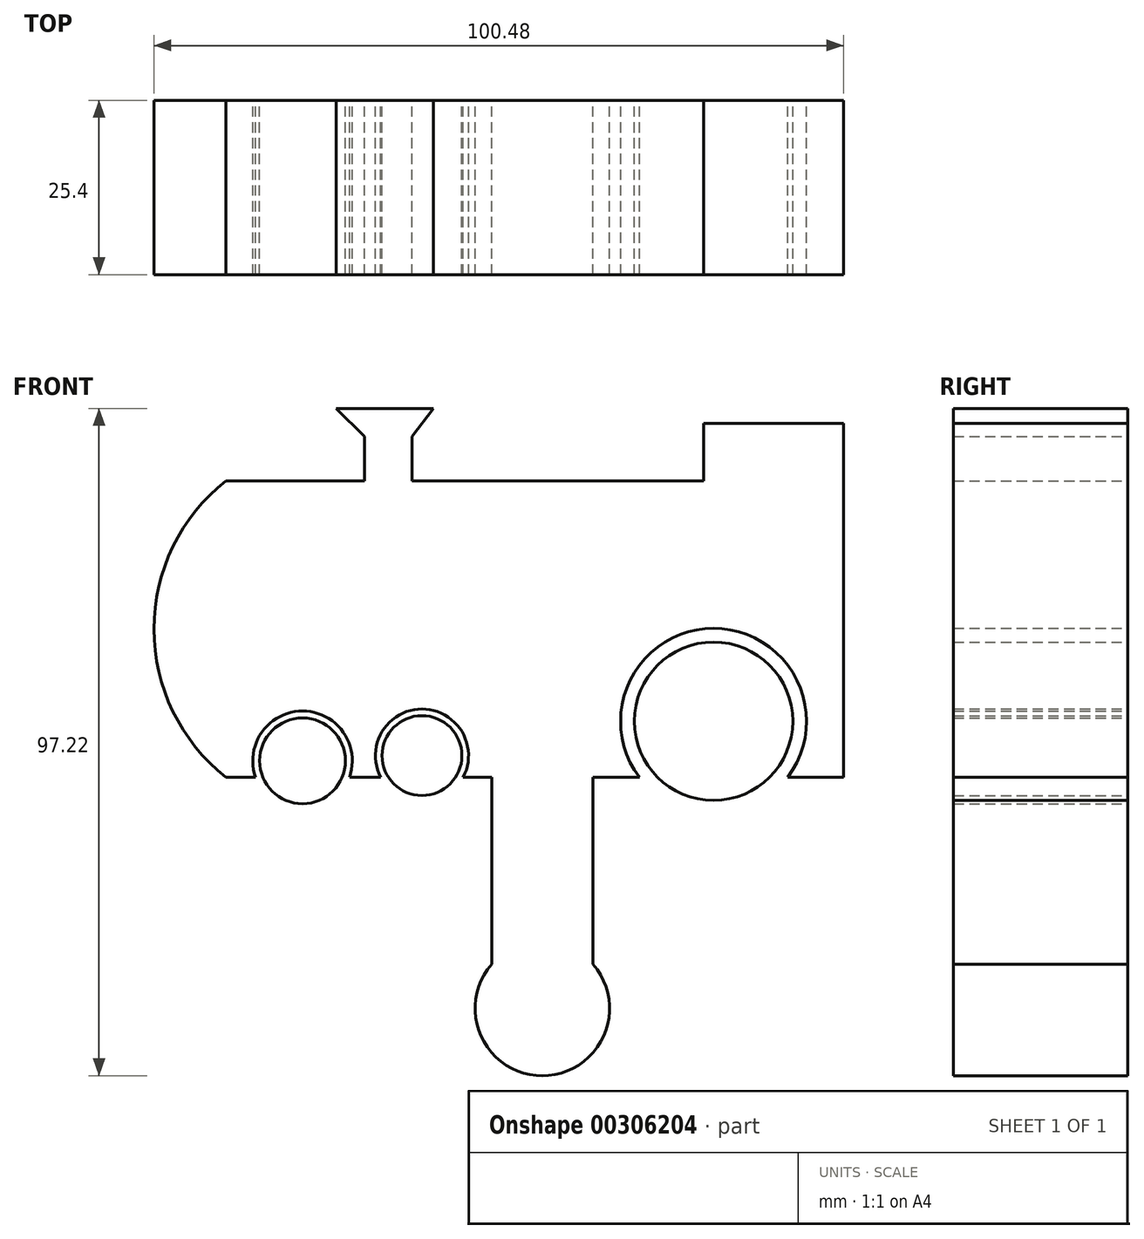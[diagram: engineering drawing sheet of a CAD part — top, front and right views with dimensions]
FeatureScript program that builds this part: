
annotation { "Feature Type Name" : "Feature", "Feature Type Description" : "" }
export const myFeature = defineFeature(function(context is Context, id is Id, definition is map)
    precondition{}
    {
        {
            var Q0;
            Q0=qCreatedBy(makeId("Front.planeOp"),FACE);
            var sketch = newSketch(context, id + "F0", { "sketchPlane" : qUnion([Q0])});
            skLineSegment(sketch, "E0", {"start": v(-7.42, 0) * mm, "end": v(-7.42, -27.23) * mm});
            skLineSegment(sketch, "E1", {"start": v(7.35, 0) * mm, "end": v(7.35, -27.23) * mm});
            skArc(sketch, "E2", {"start": v(-7.42, -27.23) * mm, "mid": v(-0.03, -43.47) * mm, "end": v(7.35, -27.23) * mm});
            skLineSegment(sketch, "E3", {"start": v(-7.42, 0) * mm, "end": v(-11.56, 0) * mm});
            skLineSegment(sketch, "E4", {"start": v(-23.56, 0) * mm, "end": v(-28.12, 0) * mm});
            skLineSegment(sketch, "E5", {"start": v(-41.8, 0) * mm, "end": v(-46.12, 0) * mm});
            skArc(sketch, "E6", {"start": v(-28.12, 0) * mm, "mid": v(-34.96, 9.65) * mm, "end": v(-41.8, 0) * mm});
            skArc(sketch, "E7", {"start": v(-11.56, 0) * mm, "mid": v(-17.56, 9.95) * mm, "end": v(-23.56, 0) * mm});
            skLineSegment(sketch, "E8", {"start": v(7.35, 0) * mm, "end": v(14.12, 0) * mm});
            skLineSegment(sketch, "E9", {"start": v(35.72, 0) * mm, "end": v(43.88, 0) * mm});
            skArc(sketch, "E10", {"start": v(35.72, 0) * mm, "mid": v(24.92, 21.7) * mm, "end": v(14.12, 0) * mm});
            skCircle(sketch, "E11", {"center": v(-34.96, 2.4) * mm, "radius": 6.25 * mm});
            skCircle(sketch, "E12", {"center": v(-17.56, 3.16) * mm, "radius": 5.82 * mm});
            skCircle(sketch, "E13", {"center": v(24.92, 8.17) * mm, "radius": 11.54 * mm});
            skLineSegment(sketch, "E14", {"start": v(43.88, 0) * mm, "end": v(43.88, 51.6) * mm});
            skLineSegment(sketch, "E15", {"start": v(43.88, 51.6) * mm, "end": v(23.48, 51.6) * mm});
            skLineSegment(sketch, "E16", {"start": v(23.48, 51.6) * mm, "end": v(23.48, 21.63) * mm});
            skLineSegment(sketch, "E17", {"start": v(23.48, 21.63) * mm, "end": v(23.48, 43.2) * mm});
            skLineSegment(sketch, "E18", {"start": v(23.48, 43.2) * mm, "end": v(-19, 43.2) * mm});
            skLineSegment(sketch, "E19", {"start": v(-19, 43.2) * mm, "end": v(-19, 49.67) * mm});
            skLineSegment(sketch, "E20", {"start": v(-19, 49.67) * mm, "end": v(-15.88, 53.75) * mm});
            skLineSegment(sketch, "E21", {"start": v(-15.88, 53.75) * mm, "end": v(-30.04, 53.75) * mm});
            skLineSegment(sketch, "E22", {"start": v(-30.04, 53.75) * mm, "end": v(-25.96, 49.67) * mm});
            skLineSegment(sketch, "E23", {"start": v(-25.96, 49.67) * mm, "end": v(-25.96, 43.2) * mm});
            skLineSegment(sketch, "E24", {"start": v(-25.96, 43.2) * mm, "end": v(-46.12, 43.2) * mm});
            skArc(sketch, "E25", {"start": v(-46.12, 43.2) * mm, "mid": v(-56.6, 21.6) * mm, "end": v(-46.12, 0) * mm});
            skSolve(sketch);
        }
        {
            var Q0;
            Q0=qCreatedBy(makeId("Front.planeOp"),FACE);
            var sketch = newSketch(context, id + "F1", { "sketchPlane" : qUnion([Q0])});
            skSolve(sketch);
        }
        {
            var Q0;
            Q0 = qSketchRegion(id + "F1", true);
            var Q1;
            Q1=makeQuery(id+"F0.imprint","IMPRINT",FACE,{"disambiguationData":[TD([[makeQuery(id+"F0.imprint","IMPRINT",EDGE,{"derivedFrom":sQuery(id+"F0.wireOp",EDGE,"E0")}),1.0]])]});
            var Q2;
            {var subQ1=sQuery(id+"F0.wireOp",EDGE,"E9");Q2=makeQuery(id+"F0.imprint","IMPRINT",FACE,{"disambiguationData":[TD([[makeQuery(id+"F0.imprint","IMPRINT",EDGE,{"derivedFrom":subQ1}),1.0]])]});}
            var Q3;
            Q3=makeQuery(id+"F0.imprint","IMPRINT",FACE,{"disambiguationData":[TD([[makeQuery(id+"F0.imprint","IMPRINT",EDGE,{"derivedFrom":sQuery(id+"F0.wireOp",EDGE,"E13")}),1.0]])]});
            var Q4;
            Q4=makeQuery(id+"F0.imprint","IMPRINT",FACE,{"disambiguationData":[TD([[makeQuery(id+"F0.imprint","IMPRINT",EDGE,{"derivedFrom":sQuery(id+"F0.wireOp",EDGE,"E12")}),1.0]])]});
            var Q5;
            Q5=makeQuery(id+"F0.imprint","IMPRINT",FACE,{"disambiguationData":[TD([[makeQuery(id+"F0.imprint","IMPRINT",EDGE,{"derivedFrom":sQuery(id+"F0.wireOp",EDGE,"E11")}),1.0]])]});
            extrude(context, id + "F2", {"entities" : qUnion([Q0, Q1, Q2, Q3, Q4, Q5]), "depth" : 25.4 * mm});
        }
    });
